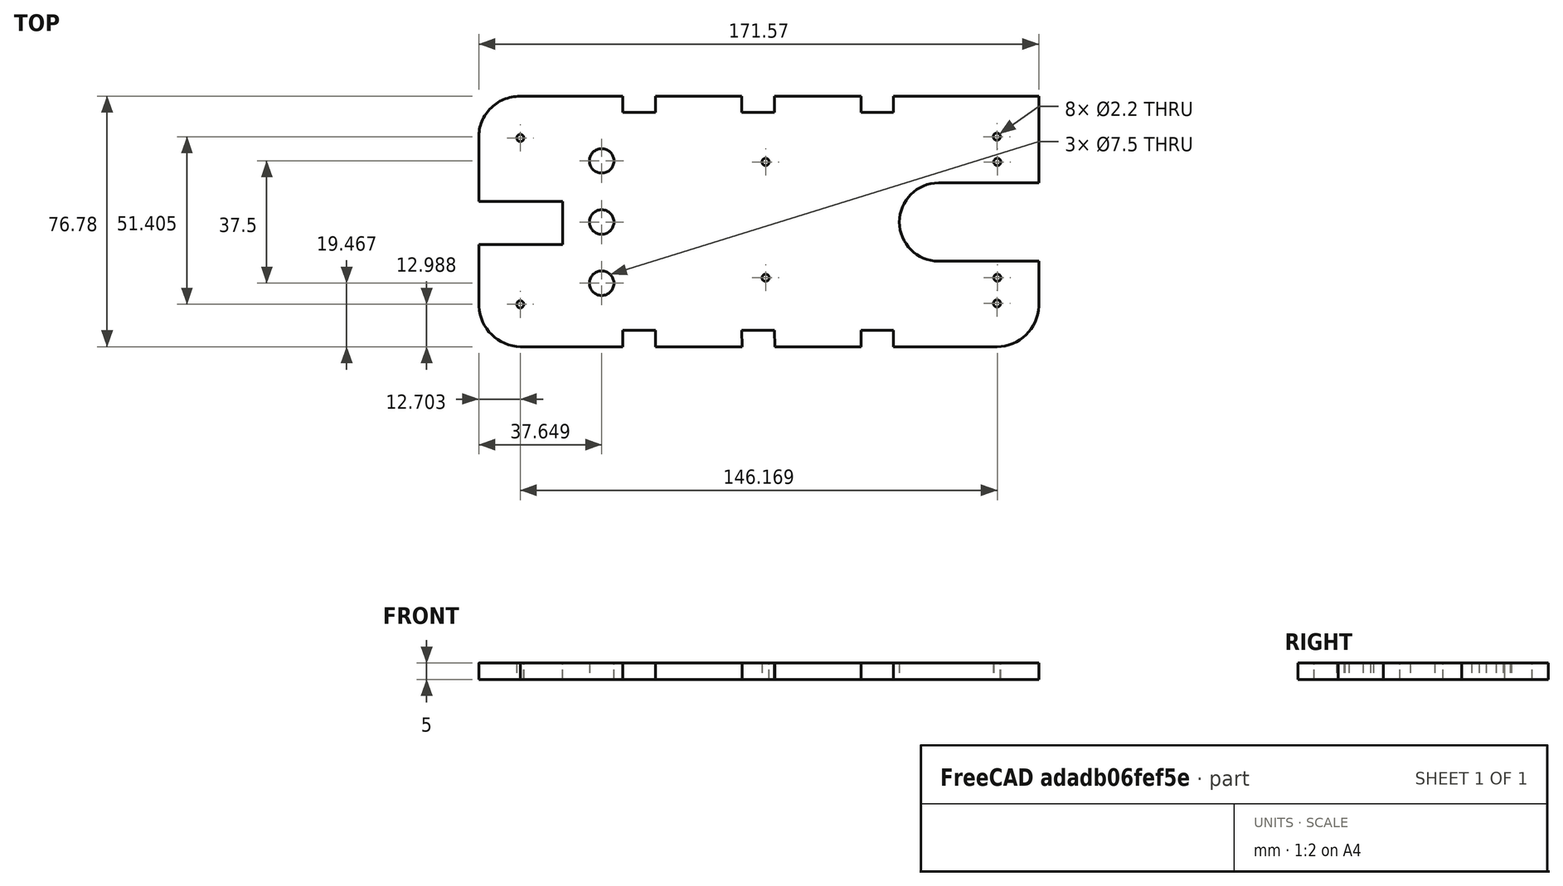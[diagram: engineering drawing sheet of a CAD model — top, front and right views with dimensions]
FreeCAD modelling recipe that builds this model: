
FCSTD DOCUMENT  (FreeCAD 1.0R38643 (Git))
Label: Acryl_B01
License: All rights reserved
LicenseURL: https://en.wikipedia.org/wiki/All_rights_reserved
objects: TechDraw::DrawViewDimension×26, Sketcher::SketchObject×1, PartDesign::Pad×1, PartDesign::Body×1, TechDraw::DrawSVGTemplate×1, TechDraw::DrawProjGroupItem×1, TechDraw::DrawPage×1
note: 51 computed .brp shape members not serialized (recipe doc carries the construction recipe); baked Part::Feature solids carry a one-line shape summary decoded from their .brp

FEATURE [Sketcher::SketchObject] Sketch
  ArcFitTolerance = 1e-06
  AttachmentSupport = -> [XY_Plane]
  FullyConstrained = false
  MakeInternals = false
  MapMode = 5
  sketch-geometry (50):
    g0: LineSegment StartX=-161.307 StartY=65.6202 StartZ=0 EndX=-161.307 EndY=40.2902 EndZ=0
    g1: LineSegment StartX=-141.207 StartY=-10.9798 StartZ=0 EndX=-108.827 EndY=-10.9798 EndZ=0
    g2: LineSegment StartX=5.62661 StartY=79.0202 StartZ=0 EndX=-25.8266 EndY=79.0202 EndZ=0
    g3: ArcOfCircle CenterX=-12.05 CenterY=34.0202 CenterZ=0 NormalX=0 NormalY=0 NormalZ=1 AngleXU=0 Radius=12 StartAngle=1.5708 EndAngle=4.71239
    g4: LineSegment StartX=18.3134 StartY=22.0202 StartZ=0 EndX=-12.05 EndY=22.0202 EndZ=0
    g5: LineSegment StartX=18.3134 StartY=46.0202 StartZ=0 EndX=-12.05 EndY=46.0202 EndZ=0
    g6: GeomPoint X=18.3134 Y=46.0202 Z=0
    g7: GeomPoint X=18.3134 Y=22.0202 Z=0
    g8: LineSegment StartX=18.3134 StartY=22.0202 StartZ=0 EndX=18.3134 EndY=14.6402 EndZ=0
    g9: LineSegment StartX=18.3134 StartY=46.0202 StartZ=0 EndX=18.3134 EndY=65.6202 EndZ=0
    g10: GeomPoint X=-115.261 Y=34.0202 Z=0
    g11: Circle CenterX=-115.261 CenterY=34.0202 CenterZ=0 NormalX=0 NormalY=0 NormalZ=1 AngleXU=0 Radius=3.75
    g12: Circle CenterX=-115.261 CenterY=52.7702 CenterZ=0 NormalX=0 NormalY=0 NormalZ=1 AngleXU=0 Radius=3.75
    g13: Circle CenterX=-115.261 CenterY=15.2702 CenterZ=0 NormalX=0 NormalY=0 NormalZ=1 AngleXU=0 Radius=3.75
    g14: LineSegment StartX=-108.82 StartY=74.0202 StartZ=0 EndX=-98.82 EndY=74.0202 EndZ=0
    g15: LineSegment StartX=-72.3266 StartY=74.0202 StartZ=0 EndX=-62.3266 EndY=74.0202 EndZ=0
    g16: LineSegment StartX=-62.3266 StartY=74.0202 StartZ=0 EndX=-62.3266 EndY=79.0202 EndZ=0
    g17: LineSegment StartX=-72.3266 StartY=79.0202 StartZ=0 EndX=-72.3266 EndY=74.0202 EndZ=0
    g18: LineSegment StartX=-35.8266 StartY=74.0202 StartZ=0 EndX=-25.8266 EndY=74.0202 EndZ=0
    g19: LineSegment StartX=-25.8266 StartY=74.0202 StartZ=0 EndX=-25.8266 EndY=79.0202 EndZ=0
    g20: LineSegment StartX=-35.8266 StartY=79.0202 StartZ=0 EndX=-35.8266 EndY=74.0202 EndZ=0
    g21: GeomPoint X=-108.82 Y=79.0202 Z=0
    g22: LineSegment StartX=-108.82 StartY=79.0202 StartZ=0 EndX=-108.82 EndY=74.0202 EndZ=0
    g23: LineSegment StartX=-98.82 StartY=74.0202 StartZ=0 EndX=-98.82 EndY=79.0202 EndZ=0
    g24: LineSegment StartX=-108.82 StartY=79.0202 StartZ=0 EndX=-139.26 EndY=79.0202 EndZ=0
    g25: LineSegment StartX=-72.3266 StartY=79.0202 StartZ=0 EndX=-98.82 EndY=79.0202 EndZ=0
    g26: LineSegment StartX=-35.8266 StartY=79.0202 StartZ=0 EndX=-62.3266 EndY=79.0202 EndZ=0
    g27: LineSegment StartX=-98.8266 StartY=-10.9798 StartZ=0 EndX=-98.82 EndY=-5.97976 EndZ=0
    g28: LineSegment StartX=-98.82 StartY=-5.97976 StartZ=0 EndX=-108.82 EndY=-5.97976 EndZ=0
    g29: LineSegment StartX=-108.82 StartY=-5.97976 StartZ=0 EndX=-108.827 EndY=-10.9798 EndZ=0
    g30: LineSegment StartX=-62.2333 StartY=-10.9798 StartZ=0 EndX=-62.3266 EndY=-5.97976 EndZ=0
    g31: LineSegment StartX=-62.3266 StartY=-5.97976 StartZ=0 EndX=-72.3266 EndY=-5.97976 EndZ=0
    g32: LineSegment StartX=-72.3266 StartY=-5.97976 StartZ=0 EndX=-72.2333 EndY=-10.9798 EndZ=0
    g33: LineSegment StartX=-25.8266 StartY=-10.9798 StartZ=0 EndX=-25.8266 EndY=-5.97976 EndZ=0
    g34: LineSegment StartX=-25.8266 StartY=-5.97976 StartZ=0 EndX=-35.8266 EndY=-5.97976 EndZ=0
    g35: LineSegment StartX=-35.8266 StartY=-5.97976 StartZ=0 EndX=-35.8266 EndY=-10.9798 EndZ=0
    g36: LineSegment StartX=-62.2333 StartY=-10.9798 StartZ=0 EndX=-35.8266 EndY=-10.9798 EndZ=0
    g37: LineSegment StartX=-98.8266 StartY=-10.9798 StartZ=0 EndX=-72.2333 EndY=-10.9798 EndZ=0
    g38: LineSegment StartX=-25.8266 StartY=-10.9798 StartZ=0 EndX=5.62661 EndY=-10.9798 EndZ=0
    g39: LineSegment StartX=-161.307 StartY=27.0902 StartZ=0 EndX=-127.2 EndY=27.0902 EndZ=0
    g40: LineSegment StartX=-127.2 StartY=27.0902 StartZ=0 EndX=-127.2 EndY=40.2902 EndZ=0
    g41: LineSegment StartX=-127.2 StartY=40.2902 StartZ=0 EndX=-161.307 EndY=40.2902 EndZ=0
    g42: LineSegment StartX=-161.307 StartY=27.0902 StartZ=0 EndX=-161.307 EndY=14.6402 EndZ=0
    g43: LineSegment StartX=-161.307 StartY=14.6402 StartZ=0 EndX=-161.307 EndY=-10.9798 EndZ=0
    g44: LineSegment StartX=-161.307 StartY=-10.9798 StartZ=0 EndX=-141.207 EndY=-10.9798 EndZ=0
    g45: ArcOfCircle CenterX=5.77038 CenterY=66.4506 CenterZ=0 NormalX=0 NormalY=0 NormalZ=1 AngleXU=0 Radius=12.5705 StartAngle=6.21708 EndAngle=7.86542
    g46: ArcOfCircle CenterX=5.63389 CenterY=1.76025 CenterZ=0 NormalX=0 NormalY=0 NormalZ=1 AngleXU=0 Radius=12.74 StartAngle=4.71182 EndAngle=6.18568
    g47: LineSegment StartX=18.3134 StartY=14.6402 StartZ=0 EndX=18.3134 EndY=0.519986 EndZ=0
    g48: ArcOfCircle CenterX=-145.354 CenterY=62.9897 CenterZ=0 NormalX=0 NormalY=0 NormalZ=1 AngleXU=0 Radius=16.1681 StartAngle=1.70134 EndAngle=2.97817
    g49: LineSegment StartX=-139.26 StartY=79.0202 StartZ=0 EndX=-147.459 EndY=79.0202 EndZ=0
  constraints (107):
    c: Coincident(g21,g22)
    c: Coincident(g21,g24)
    c: Coincident(g23,g25)
    c: Coincident(g17,g25)
    c: Coincident(g16,g26)
    c: Coincident(g20,g26)
    c: Coincident(g2,g19)
    c: Horizontal(g24,g21)
    c: Horizontal(g21,g23)
    c: Horizontal(g23,g17)
    c: Horizontal(g17,g16)
    c: Horizontal(g16,g20)
    c: Horizontal(g20,g2)
    c: Horizontal(g2,g2)
    c: Coincident(g14,g22)
    c: Equal(g23,g22)
    c: Equal(g22,g17)
    c: Equal(g17,g16)
    c: Equal(g16,g20)
    c: Equal(g20,g19)
    c: DistanceY(g14,g21) = 5
    c: Coincident(g15,g17)
    c: Coincident(g15,g16)
    c: Coincident(g18,g20)
    c: Coincident(g14,g23)
    c: Coincident(g18,g19)
    c: Coincident(g0,g41)
    c: Coincident(g39,g42)
    c: Vertical(g0,g0)
    c: Vertical(g0,g39)
    c: Vertical(g39,g42)
    c: Coincident(g40,g41)
    c: Coincident(g39,g40)
    c: Coincident(g1,g29)
    c: Coincident(g32,g37)
    c: Coincident(g27,g37)
    c: Coincident(g30,g36)
    c: Coincident(g35,g36)
    c: Coincident(g33,g38)
    c: Coincident(g28,g29)
    c: Coincident(g27,g28)
    c: Coincident(g31,g32)
    c: Coincident(g30,g31)
    c: Coincident(g34,g35)
    c: Coincident(g33,g34)
    c: Coincident(g4,g7)
    c: Coincident(g4,g8)
    c: Coincident(g5,g6)
    c: Coincident(g5,g9)
    c: Coincident(g3,g5)
    c: Coincident(g3,g4)
    c: Horizontal(g41)
    c: Horizontal(g39)
    c: DistanceY(g39,g0) = 13.2
    c: DistanceY(g4,g5) = 24
    c: DistanceY(g10,g40) = 6.27
    c: DistanceY(g10,g12) = 18.75
    c: DistanceY(g13,g10) = 18.75
    c: Horizontal(g0,g9)
    c: Horizontal(g42,g8)
    c: Horizontal(g10,g3)
    c: Horizontal(g3,g5)
    c: Horizontal(g3,g4)
    c: Horizontal(g38,g33)
    c: Horizontal(g33,g35)
    c: Horizontal(g35,g30)
    c: Horizontal(g30,g32)
    c: Horizontal(g32,g27)
    c: Horizontal(g27,g1)
    c: Horizontal(g1,g1)
    c: Horizontal(g28,g27)
    c: Horizontal(g27,g31)
    c: Horizontal(g31,g30)
    c: Horizontal(g30,g34)
    c: Horizontal(g34,g33)
    c: Vertical(g4,g8)
    c: Vertical(g9,g5)
    c: Vertical(g5,g4)
    c: Vertical(g38,g2)
    c: DistanceY(g1,g28) = 5
    c: Vertical(g3,g3)
    c: Vertical(g14,g28)
    c: Vertical(g14,g27)
    c: Vertical(g15,g31)
    c: Vertical(g15,g30)
    c: Vertical(g18,g33)
    c: Vertical(g18,g34)
    c: DistanceX(g21,g23) = 10
    c: DistanceX(g17,g16) = 10
    c: DistanceX(g20,g2) = 10
    c: Coincident(g11,g10)
    c: DistanceY(g42,g0) = 50.98
    c: DistanceY(g0,g24) = 13.4
    c: DistanceY(g1,g24) = 90
    c: Coincident(g43,g42)
    c: Coincident(g44,g43)
    c: Coincident(g44,g1)
    c: Coincident(g45,g2)
    c: Coincident(g45,g9)
    c: Coincident(g46,g38)
    c: Coincident(g47,g8)
    c: Coincident(g47,g46)
    c: Vertical(g47)
    c: Coincident(g48,g0)
    c: Coincident(g49,g24)
    c: Coincident(g49,g48)
    c: Horizontal(g49)
FEATURE [PartDesign::Pad] Pad
  Direction = (0,0,1)
  Length = 5
  Length2 = 10
  Profile = -> Sketch
  ReferenceAxis = -> Sketch [N_Axis]
  Refine = true
  Suppressed = false
  Type = 0
FEATURE [PartDesign::Body] Body
  AllowCompound = false
  Group = -> [Sketch,Pad]
  Origin = -> Origin
  Tip = -> Pad
FEATURE [TechDraw::DrawSVGTemplate] Template
  Height = 210
  Orientation = 1
  Template = <path>
  Width = 297
FEATURE [TechDraw::DrawProjGroupItem] View
  CoarseView = false
  Direction = (0,0,1)
  Focus = 100
  HardHidden = false
  IsoCount = 0
  IsoHidden = false
  IsoVisible = false
  LockPosition = false
  Perspective = false
  Rotation = 0
  RotationVector = (1,0,0)
  ScaleType = 0
  ScrubCount = 1
  SeamHidden = false
  SeamVisible = false
  SmoothHidden = false
  SmoothVisible = true
  Source = -> [Body]
  Type = 0
  X = 146.213
  XDirection = (1,0,0)
  Y = 105.457
FEATURE [TechDraw::DrawViewDimension] Dimension
  AngleOverride = false
  Arbitrary = false
  ArbitraryTolerances = false
  BoxCorners = (2) [(-85.0337,-37.7447,0),(85.0337,37.7447,0)]
  EqualTolerance = true
  ExtensionAngle = 0
  FormatSpec = %.2w
  FormatSpecOverTolerance = %+.2w
  FormatSpecUnderTolerance = %+.2w
  Inverted = false
  LineAngle = 0
  LockPosition = false
  MeasureType = 1
  OverTolerance = 0
  References2D = -> [View]
  Rotation = 0
  ScaleType = 0
  TheoreticalExact = false
  Type = 1
  UnderTolerance = 0
  X = -36.6469
  Y = 49.1205
FEATURE [TechDraw::DrawViewDimension] Dimension001
  AngleOverride = false
  Arbitrary = false
  ArbitraryTolerances = false
  BoxCorners = (2) [(-85.0337,-37.7447,0),(85.0337,37.7447,0)]
  EqualTolerance = true
  ExtensionAngle = 0
  FormatSpec = %.2w
  FormatSpecOverTolerance = %+.2w
  FormatSpecUnderTolerance = %+.2w
  Inverted = false
  LineAngle = 0
  LockPosition = false
  MeasureType = 1
  OverTolerance = 0
  References2D = -> [View]
  Rotation = 0
  ScaleType = 0
  TheoreticalExact = false
  Type = 2
  UnderTolerance = 0
  X = 10.1068
  Y = 35.6569
FEATURE [TechDraw::DrawViewDimension] Dimension002
  AngleOverride = false
  Arbitrary = false
  ArbitraryTolerances = false
  BoxCorners = (2) [(-85.0337,-37.7447,0),(85.0337,37.7447,0)]
  EqualTolerance = true
  ExtensionAngle = 0
  FormatSpec = %.2w
  FormatSpecOverTolerance = %+.2w
  FormatSpecUnderTolerance = %+.2w
  Inverted = false
  LineAngle = 0
  LockPosition = false
  MeasureType = 1
  OverTolerance = 0
  References2D = -> [View]
  Rotation = 0
  ScaleType = 0
  TheoreticalExact = false
  Type = 1
  UnderTolerance = 0
  X = -4.82983
  Y = 57.9458
FEATURE [TechDraw::DrawViewDimension] Dimension003
  AngleOverride = false
  Arbitrary = false
  ArbitraryTolerances = false
  BoxCorners = (2) [(-85.0337,-37.7447,0),(85.0337,37.7447,0)]
  EqualTolerance = true
  ExtensionAngle = 0
  FormatSpec = %.2w
  FormatSpecOverTolerance = %+.2w
  FormatSpecUnderTolerance = %+.2w
  Inverted = false
  LineAngle = 0
  LockPosition = false
  MeasureType = 1
  OverTolerance = 0
  References2D = -> [View]
  Rotation = 0
  ScaleType = 0
  TheoreticalExact = false
  Type = 2
  UnderTolerance = 0
  X = 93.5942
  Y = 0.099765
FEATURE [TechDraw::DrawViewDimension] Dimension004
  AngleOverride = false
  Arbitrary = false
  ArbitraryTolerances = false
  BoxCorners = (2) [(-85.0337,-37.7447,0),(85.0337,37.7447,0)]
  EqualTolerance = true
  ExtensionAngle = 0
  FormatSpec = %.2w
  FormatSpecOverTolerance = %+.2w
  FormatSpecUnderTolerance = %+.2w
  Inverted = false
  LineAngle = 0
  LockPosition = false
  MeasureType = 1
  OverTolerance = 0
  References2D = -> [View]
  Rotation = 0
  ScaleType = 0
  TheoreticalExact = false
  Type = 1
  UnderTolerance = 0
  X = -72.5269
  Y = 14.7383
FEATURE [TechDraw::DrawViewDimension] Dimension005
  AngleOverride = false
  Arbitrary = false
  ArbitraryTolerances = false
  BoxCorners = (2) [(-85.0337,-37.7447,0),(85.0337,37.7447,0)]
  EqualTolerance = true
  ExtensionAngle = 0
  FormatSpec = %.2w
  FormatSpecOverTolerance = %+.2w
  FormatSpecUnderTolerance = %+.2w
  Inverted = false
  LineAngle = 0
  LockPosition = false
  MeasureType = 1
  OverTolerance = 0
  References2D = -> [View]
  Rotation = 0
  ScaleType = 0
  TheoreticalExact = false
  Type = 1
  UnderTolerance = 0
  X = -54.0575
  Y = -25.8768
FEATURE [TechDraw::DrawViewDimension] Dimension006
  AngleOverride = false
  Arbitrary = false
  ArbitraryTolerances = false
  BoxCorners = (2) [(-85.0337,-37.7447,0),(85.0337,37.7447,0)]
  EqualTolerance = true
  ExtensionAngle = 0
  FormatSpec = %.2w
  FormatSpecOverTolerance = %+.2w
  FormatSpecUnderTolerance = %+.2w
  Inverted = false
  LineAngle = 0
  LockPosition = false
  MeasureType = 1
  OverTolerance = 0
  References2D = -> [View]
  Rotation = 0
  ScaleType = 0
  TheoreticalExact = false
  Type = 1
  UnderTolerance = 0
  X = -22.9764
  Y = 11.5319
FEATURE [TechDraw::DrawViewDimension] Dimension007
  AngleOverride = false
  Arbitrary = false
  ArbitraryTolerances = false
  BoxCorners = (2) [(-85.0337,-37.7447,0),(85.0337,37.7447,0)]
  EqualTolerance = true
  ExtensionAngle = 0
  FormatSpec = %.2w
  FormatSpecOverTolerance = %+.2w
  FormatSpecUnderTolerance = %+.2w
  Inverted = false
  LineAngle = 0
  LockPosition = false
  MeasureType = 1
  OverTolerance = 0
  References2D = -> [View]
  Rotation = 0
  ScaleType = 0
  TheoreticalExact = false
  Type = 1
  UnderTolerance = 0
  X = 70.0481
  Y = 7.73832
FEATURE [TechDraw::DrawViewDimension] Dimension008
  AngleOverride = false
  Arbitrary = false
  ArbitraryTolerances = false
  BoxCorners = (2) [(-85.0337,-37.7447,0),(85.0337,37.7447,0)]
  EqualTolerance = true
  ExtensionAngle = 0
  FormatSpec = %.2w
  FormatSpecOverTolerance = %+.2w
  FormatSpecUnderTolerance = %+.2w
  Inverted = false
  LineAngle = 0
  LockPosition = false
  MeasureType = 1
  OverTolerance = 0
  References2D = -> [View]
  Rotation = 0
  ScaleType = 0
  TheoreticalExact = false
  Type = 1
  UnderTolerance = 0
  X = 78.9765
  Y = 47.4304
FEATURE [TechDraw::DrawViewDimension] Dimension009
  AngleOverride = false
  Arbitrary = false
  ArbitraryTolerances = false
  BoxCorners = (2) [(-85.0337,-37.7447,0),(85.0337,37.7447,0)]
  EqualTolerance = true
  ExtensionAngle = 0
  FormatSpec = %.2w
  FormatSpecOverTolerance = %+.2w
  FormatSpecUnderTolerance = %+.2w
  Inverted = false
  LineAngle = 0
  LockPosition = false
  MeasureType = 1
  OverTolerance = 0
  References2D = -> [View]
  Rotation = 0
  ScaleType = 0
  TheoreticalExact = false
  Type = 2
  UnderTolerance = 0
  X = 56.933
  Y = 21.7837
FEATURE [TechDraw::DrawViewDimension] Dimension010
  AngleOverride = false
  Arbitrary = false
  ArbitraryTolerances = false
  BoxCorners = (2) [(-85.0337,-37.7447,0),(85.0337,37.7447,0)]
  EqualTolerance = true
  ExtensionAngle = 0
  FormatSpec = %.2w
  FormatSpecOverTolerance = %+.2w
  FormatSpecUnderTolerance = %+.2w
  Inverted = false
  LineAngle = 0
  LockPosition = false
  MeasureType = 1
  OverTolerance = 0
  References2D = -> [View]
  Rotation = 0
  ScaleType = 0
  TheoreticalExact = false
  Type = 2
  UnderTolerance = 0
  X = -15.9972
  Y = 25.7819
FEATURE [TechDraw::DrawViewDimension] Dimension011
  AngleOverride = false
  Arbitrary = false
  ArbitraryTolerances = false
  BoxCorners = (2) [(-85.0337,-37.7447,0),(85.0337,37.7447,0)]
  EqualTolerance = true
  ExtensionAngle = 0
  FormatSpec = %.2w
  FormatSpecOverTolerance = %+.2w
  FormatSpecUnderTolerance = %+.2w
  Inverted = false
  LineAngle = 0
  LockPosition = false
  MeasureType = 1
  OverTolerance = 0
  References2D = -> [View]
  Rotation = 0
  ScaleType = 0
  TheoreticalExact = false
  Type = 2
  UnderTolerance = 0
  X = 10.1068
  Y = -25.4681
FEATURE [TechDraw::DrawViewDimension] Dimension012
  AngleOverride = false
  Arbitrary = false
  ArbitraryTolerances = false
  BoxCorners = (2) [(-85.0337,-37.7447,0),(85.0337,37.7447,0)]
  EqualTolerance = true
  ExtensionAngle = 0
  FormatSpec = %.2w
  FormatSpecOverTolerance = %+.2w
  FormatSpecUnderTolerance = %+.2w
  Inverted = false
  LineAngle = 0
  LockPosition = false
  MeasureType = 1
  OverTolerance = 0
  References2D = -> [View]
  Rotation = 0
  ScaleType = 0
  TheoreticalExact = false
  Type = 2
  UnderTolerance = 0
  X = 102.236
  Y = 0.156918
FEATURE [TechDraw::DrawViewDimension] Dimension013
  AngleOverride = false
  Arbitrary = false
  ArbitraryTolerances = false
  BoxCorners = (2) [(-85.0337,-37.7447,0),(85.0337,37.7447,0)]
  EqualTolerance = true
  ExtensionAngle = 0
  FormatSpec = %.2w
  FormatSpecOverTolerance = %+.2w
  FormatSpecUnderTolerance = %+.2w
  Inverted = false
  LineAngle = 0
  LockPosition = false
  MeasureType = 1
  OverTolerance = 0
  References2D = -> [View]
  Rotation = 0
  ScaleType = 0
  TheoreticalExact = false
  Type = 2
  UnderTolerance = 0
  X = 76.167
  Y = 31.6605
FEATURE [TechDraw::DrawViewDimension] Dimension014
  AngleOverride = false
  Arbitrary = false
  ArbitraryTolerances = false
  BoxCorners = (2) [(-85.0337,-37.7447,0),(85.0337,37.7447,0)]
  EqualTolerance = true
  ExtensionAngle = 0
  FormatSpec = %.2w
  FormatSpecOverTolerance = %+.2w
  FormatSpecUnderTolerance = %+.2w
  Inverted = false
  LineAngle = 0
  LockPosition = false
  MeasureType = 1
  OverTolerance = 0
  References2D = -> [View]
  Rotation = 0
  ScaleType = 0
  TheoreticalExact = false
  Type = 1
  UnderTolerance = 0
  X = -63.3369
  Y = 47.4304
FEATURE [TechDraw::DrawViewDimension] Dimension015
  AngleOverride = false
  Arbitrary = false
  ArbitraryTolerances = false
  BoxCorners = (2) [(-85.0337,-37.7447,0),(85.0337,37.7447,0)]
  EqualTolerance = true
  ExtensionAngle = 0
  FormatSpec = %.2w
  FormatSpecOverTolerance = %+.2w
  FormatSpecUnderTolerance = %+.2w
  Inverted = false
  LineAngle = 0
  LockPosition = false
  MeasureType = 1
  OverTolerance = 0
  References2D = -> [View]
  Rotation = 0
  ScaleType = 0
  TheoreticalExact = false
  Type = 1
  UnderTolerance = 0
  X = -18.4002
  Y = 47.4304
FEATURE [TechDraw::DrawViewDimension] Dimension016
  AngleOverride = false
  Arbitrary = false
  ArbitraryTolerances = false
  BoxCorners = (2) [(-85.0337,-37.7447,0),(85.0337,37.7447,0)]
  EqualTolerance = true
  ExtensionAngle = 0
  FormatSpec = %.2w
  FormatSpecOverTolerance = %+.2w
  FormatSpecUnderTolerance = %+.2w
  Inverted = false
  LineAngle = 0
  LockPosition = false
  MeasureType = 1
  OverTolerance = 0
  References2D = -> [View]
  Rotation = 0
  ScaleType = 0
  TheoreticalExact = false
  Type = 1
  UnderTolerance = 0
  X = 18.0965
  Y = 49.1205
FEATURE [TechDraw::DrawViewDimension] Dimension017
  AngleOverride = false
  Arbitrary = false
  ArbitraryTolerances = false
  BoxCorners = (2) [(-85.0337,-37.7447,0),(85.0337,37.7447,0)]
  EqualTolerance = true
  ExtensionAngle = 0
  FormatSpec = %.2w
  FormatSpecOverTolerance = %+.2w
  FormatSpecUnderTolerance = %+.2w
  Inverted = false
  LineAngle = 0
  LockPosition = false
  MeasureType = 1
  OverTolerance = 0
  References2D = -> [View]
  Rotation = 0
  ScaleType = 0
  TheoreticalExact = false
  Type = 2
  UnderTolerance = 0
  X = -94.2844
  Y = 0.149259
FEATURE [TechDraw::DrawViewDimension] Dimension018
  AngleOverride = false
  Arbitrary = false
  ArbitraryTolerances = false
  BoxCorners = (2) [(-85.0337,-37.7447,0),(85.0337,37.7447,0)]
  EqualTolerance = true
  ExtensionAngle = 0
  FormatSpec = %.2w
  FormatSpecOverTolerance = %+.2w
  FormatSpecUnderTolerance = %+.2w
  Inverted = false
  LineAngle = 0
  LockPosition = false
  MeasureType = 1
  OverTolerance = 0
  References2D = -> [View]
  Rotation = 0
  ScaleType = 0
  TheoreticalExact = false
  Type = 2
  UnderTolerance = 0
  X = -35.4019
  Y = -9.21808
FEATURE [TechDraw::DrawViewDimension] Dimension019
  AngleOverride = false
  Arbitrary = false
  ArbitraryTolerances = false
  BoxCorners = (2) [(-85.0337,-37.7447,0),(85.0337,37.7447,0)]
  EqualTolerance = true
  ExtensionAngle = 0
  FormatSpec = ⌀%.2w
  FormatSpecOverTolerance = %+.2w
  FormatSpecUnderTolerance = %+.2w
  Inverted = false
  LineAngle = 0
  LockPosition = false
  MeasureType = 1
  OverTolerance = 0
  References2D = -> [View]
  Rotation = 0
  ScaleType = 0
  TheoreticalExact = false
  Type = 5
  UnderTolerance = 0
  X = -54.3844
  Y = 29.582
FEATURE [TechDraw::DrawViewDimension] Dimension020
  AngleOverride = false
  Arbitrary = false
  ArbitraryTolerances = false
  BoxCorners = (2) [(-85.0337,-37.7447,0),(85.0337,37.7447,0)]
  EqualTolerance = true
  ExtensionAngle = 0
  FormatSpec = ⌀%.2w
  FormatSpecOverTolerance = %+.2w
  FormatSpecUnderTolerance = %+.2w
  Inverted = false
  LineAngle = 0
  LockPosition = false
  MeasureType = 1
  OverTolerance = 0
  References2D = -> [View]
  Rotation = 0
  ScaleType = 0
  TheoreticalExact = false
  Type = 5
  UnderTolerance = 0
  X = 15.1278
  Y = 14.211
FEATURE [TechDraw::DrawViewDimension] Dimension021
  AngleOverride = false
  Arbitrary = false
  ArbitraryTolerances = false
  BoxCorners = (2) [(-85.0337,-37.7447,0),(85.0337,37.7447,0)]
  EqualTolerance = true
  ExtensionAngle = 0
  FormatSpec = ⌀%.2w
  FormatSpecOverTolerance = %+.2w
  FormatSpecUnderTolerance = %+.2w
  Inverted = false
  LineAngle = 0
  LockPosition = false
  MeasureType = 1
  OverTolerance = 0
  References2D = -> [View]
  Rotation = 0
  ScaleType = 0
  TheoreticalExact = false
  Type = 5
  UnderTolerance = 0
  X = 1.23689
  Y = -5.50976
FEATURE [TechDraw::DrawViewDimension] Dimension022
  AngleOverride = false
  Arbitrary = false
  ArbitraryTolerances = false
  BoxCorners = (2) [(-85.0337,-37.7447,0),(85.0337,37.7447,0)]
  EqualTolerance = true
  ExtensionAngle = 0
  FormatSpec = ⌀%.2w
  FormatSpecOverTolerance = %+.2w
  FormatSpecUnderTolerance = %+.2w
  Inverted = false
  LineAngle = 0
  LockPosition = false
  MeasureType = 1
  OverTolerance = 0
  References2D = -> [View]
  Rotation = 0
  ScaleType = 0
  TheoreticalExact = false
  Type = 5
  UnderTolerance = 0
  X = 60.3223
  Y = -16.6003
FEATURE [TechDraw::DrawViewDimension] Dimension023
  AngleOverride = false
  Arbitrary = false
  ArbitraryTolerances = false
  BoxCorners = (2) [(-85.0337,-37.7447,0),(85.0337,37.7447,0)]
  EqualTolerance = true
  ExtensionAngle = 0
  FormatSpec = ⌀%.2w
  FormatSpecOverTolerance = %+.2w
  FormatSpecUnderTolerance = %+.2w
  Inverted = false
  LineAngle = 0
  LockPosition = false
  MeasureType = 1
  OverTolerance = 0
  References2D = -> [View]
  Rotation = 0
  ScaleType = 0
  TheoreticalExact = false
  Type = 5
  UnderTolerance = 0
  X = 59.9007
  Y = -28.1886
FEATURE [TechDraw::DrawViewDimension] Dimension024
  AngleOverride = false
  Arbitrary = false
  ArbitraryTolerances = false
  BoxCorners = (2) [(-85.0337,-37.7447,0),(85.0337,37.7447,0)]
  EqualTolerance = true
  ExtensionAngle = 0
  FormatSpec = ⌀%.2w
  FormatSpecOverTolerance = %+.2w
  FormatSpecUnderTolerance = %+.2w
  Inverted = false
  LineAngle = 0
  LockPosition = false
  MeasureType = 1
  OverTolerance = 0
  References2D = -> [View]
  Rotation = 0
  ScaleType = 0
  TheoreticalExact = false
  Type = 5
  UnderTolerance = 0
  X = -71.4276
  Y = -16.794
FEATURE [TechDraw::DrawViewDimension] Dimension025
  AngleOverride = false
  Arbitrary = false
  ArbitraryTolerances = false
  BoxCorners = (2) [(-85.0337,-37.7447,0),(85.0337,37.7447,0)]
  EqualTolerance = true
  ExtensionAngle = 0
  FormatSpec = ⌀%.2w
  FormatSpecOverTolerance = %+.2w
  FormatSpecUnderTolerance = %+.2w
  Inverted = false
  LineAngle = 0
  LockPosition = false
  MeasureType = 1
  OverTolerance = 0
  References2D = -> [View]
  Rotation = 0
  ScaleType = 0
  TheoreticalExact = false
  Type = 5
  UnderTolerance = 0
  X = -64.1366
  Y = 22.7694
FEATURE [TechDraw::DrawPage] Page
  KeepUpdated = true
  NextBalloonIndex = 1
  ProjectionType = 0
  Template = -> Template
  Views = -> [View,Dimension,Dimension001,Dimension002,Dimension003,Dimension004,Dimension005,Dimension006,Dimension007,Dimension008,Dimension009,Dimension010,Dimension011,Dimension012,Dimension013,Dimension014,Dimension015,Dimension016,Dimension017,Dimension018,Dimension019,Dimension020,Dimension021,Dimension022,Dimension023,Dimension024,Dimension025]
note: 1 file-system path scrubbed to <path> (originals preserved in the JSON sidecar)
